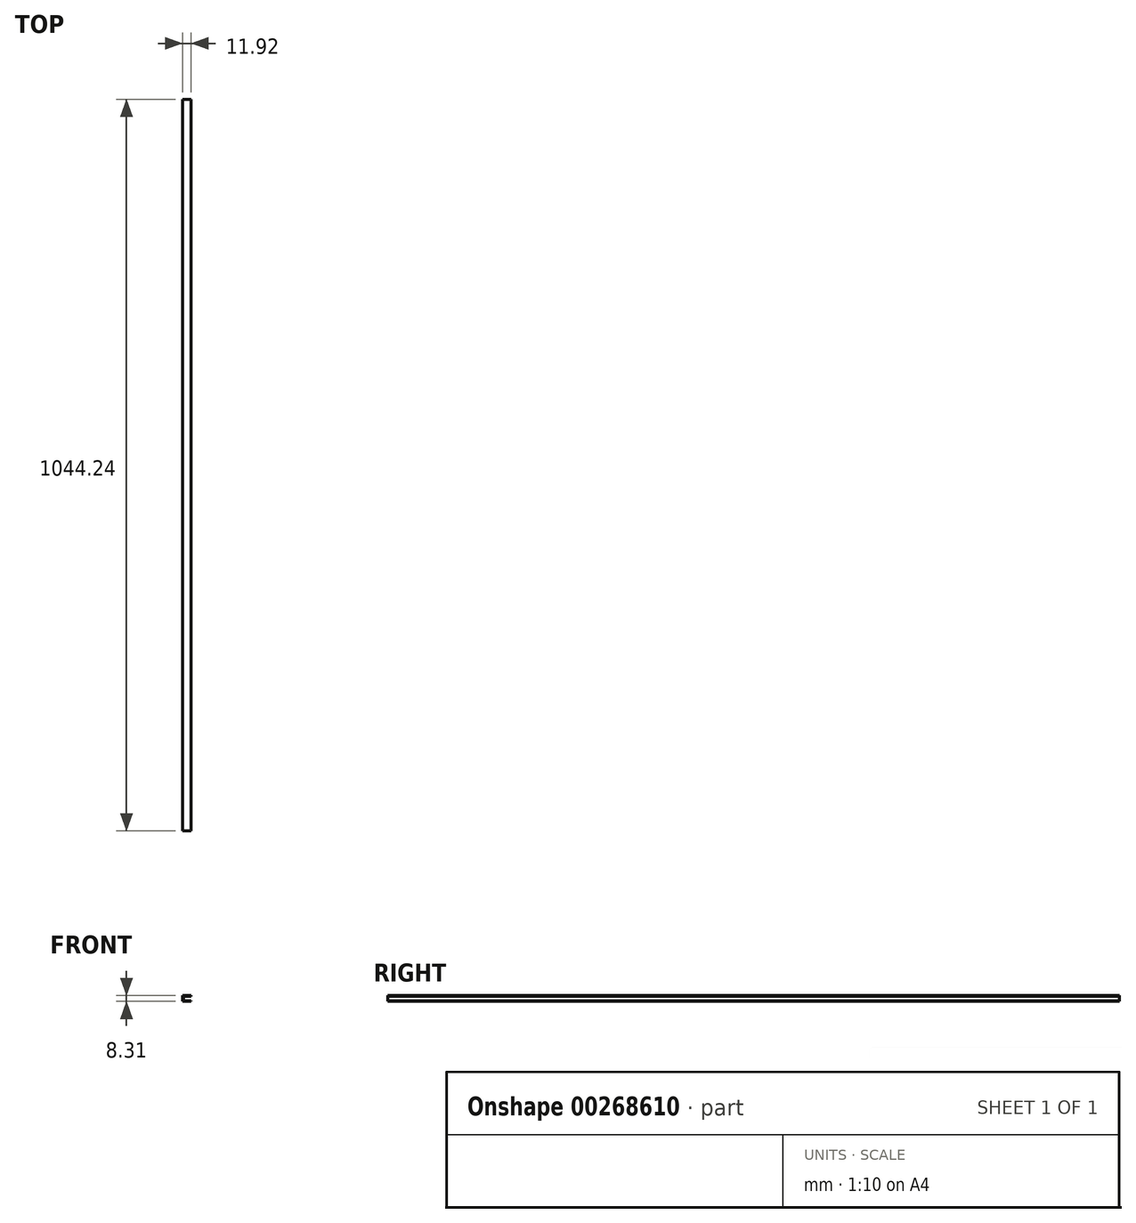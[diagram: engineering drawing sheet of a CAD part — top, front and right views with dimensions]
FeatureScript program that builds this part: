
annotation { "Feature Type Name" : "Feature", "Feature Type Description" : "" }
export const myFeature = defineFeature(function(context is Context, id is Id, definition is map)
    precondition{}
    {
        {
            var Q0;
            Q0=qCreatedBy(makeId("Front.planeOp"),FACE);
            var sketch = newSketch(context, id + "F0", { "sketchPlane" : qUnion([Q0])});
            skLineSegment(sketch, "E0.bottom", {"start": v(0, 3.35) * mm, "end": v(10.9, 3.35) * mm});
            skLineSegment(sketch, "E0.top", {"start": v(0, -3.37) * mm, "end": v(10.9, -3.37) * mm});
            skLineSegment(sketch, "E0.left", {"start": v(0, 3.35) * mm, "end": v(0, -3.37) * mm});
            skLineSegment(sketch, "E1.bottom", {"start": v(-1.02, 4.14) * mm, "end": v(10.9, 4.14) * mm});
            skLineSegment(sketch, "E1.top", {"start": v(-1.02, -4.17) * mm, "end": v(10.9, -4.17) * mm});
            skLineSegment(sketch, "E1.left", {"start": v(-1.02, 4.14) * mm, "end": v(-1.02, -4.17) * mm});
            skLineSegment(sketch, "E2", {"start": v(10.9, 3.35) * mm, "end": v(10.9, 4.14) * mm});
            skLineSegment(sketch, "E3", {"start": v(10.9, -3.37) * mm, "end": v(10.9, -4.17) * mm});
            skSolve(sketch);
        }
        {
            var Q0;
            Q0=makeQuery(id+"F0.imprint","IMPRINT",FACE,{"disambiguationData":[TD([[makeQuery(id+"F0.imprint","IMPRINT",EDGE,{"derivedFrom":sQuery(id+"F0.wireOp",EDGE,"E0.bottom")}),1.0]])]});
            extrude(context, id + "F1", {"entities" : qUnion([Q0]), "depth" : 1044.24 * mm});
        }
    });
